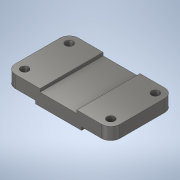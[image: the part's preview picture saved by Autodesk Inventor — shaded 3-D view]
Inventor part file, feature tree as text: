
AUTODESK INVENTOR PART (.ipt)
format: ipt  version: 2020 (Build 240168000, 168)  size: 217,088 bytes
history: native  units: mm
features: extrude x3, sketch x2, fillet x2, mirror x1
ambient origin geometry x8: Origin, YZ Plane, XZ Plane, XY Plane, X Axis, Y Axis, Z Axis, Center Point
bodies: Solid1 (feature_tree)
feature tree (8):
  extrude  "Extrusion1"  Depth=4.0mm
  sketch  "Sketch2"  dims[d2=38.0mm d3=16.0mm d4=44.0mm d5=4.0mm d6=82.0mm d7=0.0mm d8=10.0mm d9=10.0mm d10=12.0mm d11=12.0mm d12=12.0mm d13=12.0mm d14=82.0mm d15=0.0mm d16=82.0mm d17=0.0mm d18=12.0mm d19=12.0mm]
  extrude  "Extrusion2"  Depth=16.0mm
  extrude  "Extrusion3"  Depth=44.0mm
  fillet  "Fillet1"  Radius=4.0mm
  fillet  "Fillet2"  Radius=82.0mm
  mirror  "Mirror1"
  sketch  "Sketch1"  dims[d0=30.0mm d1=4.0mm]
